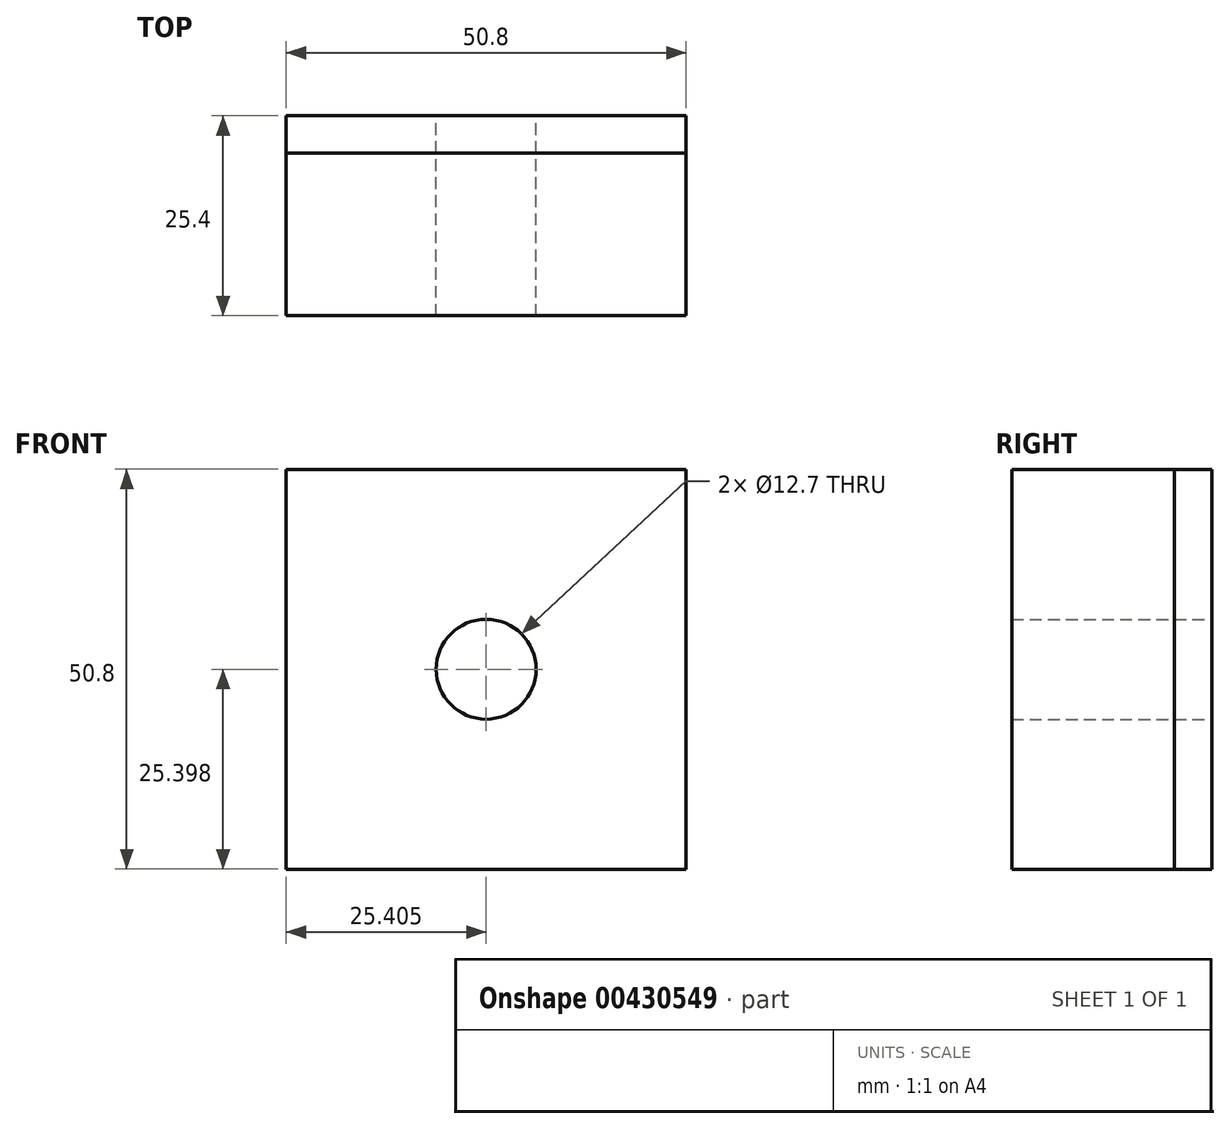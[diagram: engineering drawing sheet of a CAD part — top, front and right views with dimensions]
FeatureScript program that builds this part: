
annotation { "Feature Type Name" : "Feature", "Feature Type Description" : "" }
export const myFeature = defineFeature(function(context is Context, id is Id, definition is map)
    precondition{}
    {
        {
            var Q0;
            Q0=qCreatedBy(makeId("Front.planeOp"),FACE);
            var sketch = newSketch(context, id + "F0", { "sketchPlane" : qUnion([Q0])});
            skLineSegment(sketch, "E0.bottom", {"start": v(-27.66, 38.66) * mm, "end": v(23.14, 38.66) * mm});
            skLineSegment(sketch, "E0.top", {"start": v(-27.66, -12.14) * mm, "end": v(23.14, -12.14) * mm});
            skLineSegment(sketch, "E0.left", {"start": v(-27.66, 38.66) * mm, "end": v(-27.66, -12.14) * mm});
            skLineSegment(sketch, "E0.right", {"start": v(23.14, 38.66) * mm, "end": v(23.14, -12.14) * mm});
            skPoint(sketch, "E1", {"position": v(-27.66, 13.26) * mm});
            skPoint(sketch, "E2", {"position": v(0, 38.66) * mm});
            skPoint(sketch, "E2.positionSnap0", {"position": v(-2.26, 38.66) * mm});
            skPoint(sketch, "E3", {"position": v(-2.26, 13.26) * mm});
            skCircle(sketch, "E4", {"center": v(-2.26, 13.26) * mm, "radius": 6.35 * mm});
            skSolve(sketch);
        }
        {
            var Q0;
            Q0=makeQuery(id+"F0.imprint","IMPRINT",FACE,{"disambiguationData":[TD([[makeQuery(id+"F0.imprint","IMPRINT",EDGE,{"derivedFrom":sQuery(id+"F0.wireOp",EDGE,"E0.bottom")}),-1.0]])]});
            extrude(context, id + "F1", {"entities" : qUnion([Q0]), "depth" : 4.76 * mm});
        }
        {
            var Q0;
            Q0=makeQuery(id+"F0.imprint","IMPRINT",FACE,{"disambiguationData":[TD([[makeQuery(id+"F0.imprint","IMPRINT",EDGE,{"derivedFrom":sQuery(id+"F0.wireOp",EDGE,"E0.bottom")}),-1.0]])]});
            extrude(context, id + "F2", {"entities" : qUnion([Q0]), "depth" : 25.4 * mm});
        }
    });
